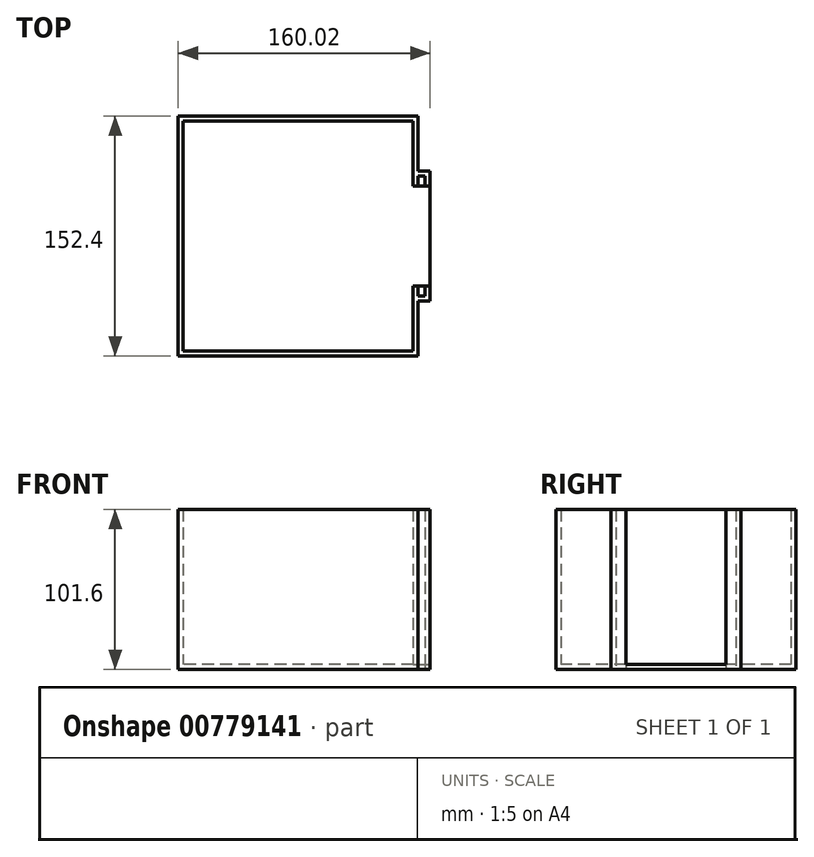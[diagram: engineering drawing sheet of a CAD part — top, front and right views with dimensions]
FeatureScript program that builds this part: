
annotation { "Feature Type Name" : "Feature", "Feature Type Description" : "" }
export const myFeature = defineFeature(function(context is Context, id is Id, definition is map)
    precondition{}
    {
        {
            var Q0;
            Q0=qCreatedBy(makeId("Top.planeOp"),FACE);
            var sketch = newSketch(context, id + "F0", { "sketchPlane" : qUnion([Q0])});
            skLineSegment(sketch, "E0.bottom", {"start": v(-76.2, 73.02) * mm, "end": v(-73.03, 73.02) * mm});
            skLineSegment(sketch, "E0.top", {"start": v(-76.2, -73.03) * mm, "end": v(-73.03, -73.03) * mm});
            skLineSegment(sketch, "E0.left", {"start": v(-73.03, 73.03) * mm, "end": v(-73.03, -73.03) * mm});
            skLineSegment(sketch, "E0.right", {"start": v(-76.2, 73.02) * mm, "end": v(-76.2, -73.02) * mm});
            skLineSegment(sketch, "E1.bottom", {"start": v(-76.2, 76.2) * mm, "end": v(76.2, 76.2) * mm});
            skLineSegment(sketch, "E1.top", {"start": v(-76.2, 73.03) * mm, "end": v(76.2, 73.03) * mm});
            skLineSegment(sketch, "E1.left", {"start": v(-76.2, 76.2) * mm, "end": v(-76.2, 73.02) * mm});
            skLineSegment(sketch, "E1.right", {"start": v(76.2, 76.2) * mm, "end": v(76.2, 73.02) * mm});
            skLineSegment(sketch, "E2.MirrorCS", {"start": v(-76.2, -73.03) * mm, "end": v(76.2, -73.02) * mm});
            skLineSegment(sketch, "E3.MirrorCS", {"start": v(-76.2, -76.2) * mm, "end": v(-76.2, -73.02) * mm});
            skLineSegment(sketch, "E4.MirrorCS", {"start": v(76.2, -76.2) * mm, "end": v(76.2, -73.02) * mm});
            skLineSegment(sketch, "E5.MirrorCS", {"start": v(-76.2, -76.2) * mm, "end": v(76.2, -76.2) * mm});
            skLineSegment(sketch, "E6.bottom", {"start": v(76.2, -73.02) * mm, "end": v(73.03, -73.02) * mm});
            skLineSegment(sketch, "E6.top", {"start": v(76.2, -31.75) * mm, "end": v(73.03, -31.75) * mm});
            skLineSegment(sketch, "E6.left", {"start": v(76.2, -73.02) * mm, "end": v(76.2, -31.75) * mm});
            skLineSegment(sketch, "E6.right", {"start": v(73.03, -73.02) * mm, "end": v(73.03, -31.75) * mm});
            skLineSegment(sketch, "E7.MirrorCS", {"start": v(73.03, 73.02) * mm, "end": v(73.03, 31.75) * mm});
            skLineSegment(sketch, "E8.MirrorCS", {"start": v(76.2, 73.02) * mm, "end": v(76.2, 31.75) * mm});
            skLineSegment(sketch, "E9.MirrorCS", {"start": v(76.2, 31.75) * mm, "end": v(73.03, 31.75) * mm});
            skLineSegment(sketch, "E10.bottom", {"start": v(76.2, 38.1) * mm, "end": v(83.82, 38.1) * mm});
            skLineSegment(sketch, "E10.top", {"start": v(76.2, 41.27) * mm, "end": v(83.82, 41.27) * mm});
            skLineSegment(sketch, "E10.left", {"start": v(76.2, 38.1) * mm, "end": v(76.2, 41.27) * mm});
            skLineSegment(sketch, "E10.right", {"start": v(83.82, 38.1) * mm, "end": v(83.82, 41.27) * mm});
            skLineSegment(sketch, "E11.bottom", {"start": v(83.82, 38.1) * mm, "end": v(80.65, 38.1) * mm});
            skLineSegment(sketch, "E11.top", {"start": v(83.82, 31.75) * mm, "end": v(80.65, 31.75) * mm});
            skLineSegment(sketch, "E11.left", {"start": v(83.82, 38.1) * mm, "end": v(83.82, 31.75) * mm});
            skLineSegment(sketch, "E11.right", {"start": v(80.65, 38.1) * mm, "end": v(80.65, 31.75) * mm});
            skLineSegment(sketch, "E12.MirrorCS", {"start": v(76.2, -41.27) * mm, "end": v(83.82, -41.27) * mm});
            skLineSegment(sketch, "E13.MirrorCS", {"start": v(83.82, -38.1) * mm, "end": v(83.82, -41.27) * mm});
            skLineSegment(sketch, "E14.MirrorCS", {"start": v(76.2, -38.1) * mm, "end": v(83.82, -38.1) * mm});
            skLineSegment(sketch, "E15.MirrorCS", {"start": v(80.65, -38.1) * mm, "end": v(80.65, -31.75) * mm});
            skLineSegment(sketch, "E16.MirrorCS", {"start": v(83.82, -38.1) * mm, "end": v(83.82, -31.75) * mm});
            skLineSegment(sketch, "E17.MirrorCS", {"start": v(83.82, -31.75) * mm, "end": v(80.65, -31.75) * mm});
            skSolve(sketch);
        }
        {
            var Q0;
            {var subQ0=sQuery(id+"F0.wireOp",EDGE,"E0.bottom");var subQ1=makeQuery(id+"F0.imprint","IMPRINT",EDGE,{"derivedFrom":subQ0});var subQ2=sQuery(id+"F0.wireOp",EDGE,"E0.top");var subQ3=makeQuery(id+"F0.imprint","IMPRINT",EDGE,{"derivedFrom":subQ2});var subQ5=sQuery(id+"F0.wireOp",EDGE,"E10.top");var subQ19=sQuery(id+"F0.wireOp",EDGE,"E7.MirrorCS");var subQ26=sQuery(id+"F0.wireOp",EDGE,"E15.MirrorCS");var subQ31=sQuery(id+"F0.wireOp",EDGE,"E12.MirrorCS");var subQ40=sQuery(id+"F0.wireOp",EDGE,"E6.top");Q0=qUnion([makeQuery(id+"F0.imprint","IMPRINT",FACE,{"disambiguationData":[TD([[subQ1,1.0]])]}),makeQuery(id+"F0.imprint","IMPRINT",FACE,{"disambiguationData":[TD([[makeQuery(id+"F0.imprint","IMPRINT",EDGE,{"derivedFrom":subQ40}),1.0]])]}),makeQuery(id+"F0.imprint","IMPRINT",FACE,{"disambiguationData":[TD([[makeQuery(id+"F0.imprint","IMPRINT",EDGE,{"derivedFrom":sQuery(id+"F0.wireOp",EDGE,"E11.top")}),-1.0]])]}),makeQuery(id+"F0.imprint","IMPRINT",FACE,{"disambiguationData":[TD([[subQ3,-1.0]])]}),makeQuery(id+"F0.imprint","IMPRINT",FACE,{"disambiguationData":[TD([[makeQuery(id+"F0.imprint","IMPRINT",EDGE,{"derivedFrom":subQ31}),1.0]])]}),makeQuery(id+"F0.imprint","IMPRINT",FACE,{"disambiguationData":[TD([[makeQuery(id+"F0.imprint","IMPRINT",EDGE,{"derivedFrom":subQ26}),-1.0]])]}),makeQuery(id+"F0.imprint","IMPRINT",FACE,{"disambiguationData":[TD([[makeQuery(id+"F0.imprint","IMPRINT",EDGE,{"derivedFrom":subQ19}),1.0]])]}),makeQuery(id+"F0.imprint","IMPRINT",FACE,{"disambiguationData":[TD([[makeQuery(id+"F0.imprint","IMPRINT",EDGE,{"derivedFrom":subQ5}),-1.0]])]}),makeQuery(id+"F0.imprint","IMPRINT",FACE,{"disambiguationData":[TD([[subQ1,-1.0]])]})]);}
            extrude(context, id + "F1", {"entities" : qUnion([Q0]), "depth" : 101.6 * mm, "offsetDistance" : 25.4 * mm});
        }
        {
            var Q0;
            Q0=qCreatedBy(makeId("Top.planeOp"),FACE);
            var sketch = newSketch(context, id + "F2", { "sketchPlane" : qUnion([Q0])});
            skLineSegment(sketch, "E18.bottom", {"start": v(73.03, 73.03) * mm, "end": v(-73.03, 73.03) * mm});
            skLineSegment(sketch, "E18.top", {"start": v(73.03, -73.03) * mm, "end": v(-73.03, -73.03) * mm});
            skLineSegment(sketch, "E18.left", {"start": v(73.03, 73.03) * mm, "end": v(73.03, -73.03) * mm});
            skLineSegment(sketch, "E18.right", {"start": v(-73.03, 73.03) * mm, "end": v(-73.03, -73.03) * mm});
            skPoint(sketch, "E18.middle", {"position": v(0, 0) * mm});
            skLineSegment(sketch, "E19.bottom", {"start": v(73.03, -31.75) * mm, "end": v(83.82, -31.75) * mm});
            skLineSegment(sketch, "E19.top", {"start": v(73.03, 31.75) * mm, "end": v(83.82, 31.75) * mm});
            skLineSegment(sketch, "E19.left", {"start": v(73.03, -31.75) * mm, "end": v(73.03, 31.75) * mm});
            skLineSegment(sketch, "E19.right", {"start": v(83.82, -31.75) * mm, "end": v(83.82, 31.75) * mm});
            skSolve(sketch);
        }
        {
            var Q0;
            {var subQ3=sQuery(id+"F2.wireOp",EDGE,"E19.bottom");var subQ7=sQuery(id+"F2.wireOp",EDGE,"E18.bottom");Q0=qUnion([makeQuery(id+"F2.imprint","IMPRINT",FACE,{"disambiguationData":[TD([[makeQuery(id+"F2.imprint","IMPRINT",EDGE,{"derivedFrom":subQ7}),1.0]])]}),makeQuery(id+"F2.imprint","IMPRINT",FACE,{"disambiguationData":[TD([[makeQuery(id+"F2.imprint","IMPRINT",EDGE,{"derivedFrom":subQ3}),1.0]])]})]);}
            extrude(context, id + "F3", {"entities" : qUnion([Q0]), "operationType" : NewBodyOperationType.ADD, "depth" : 3.17 * mm, "offsetDistance" : 25.4 * mm});
        }
    });
